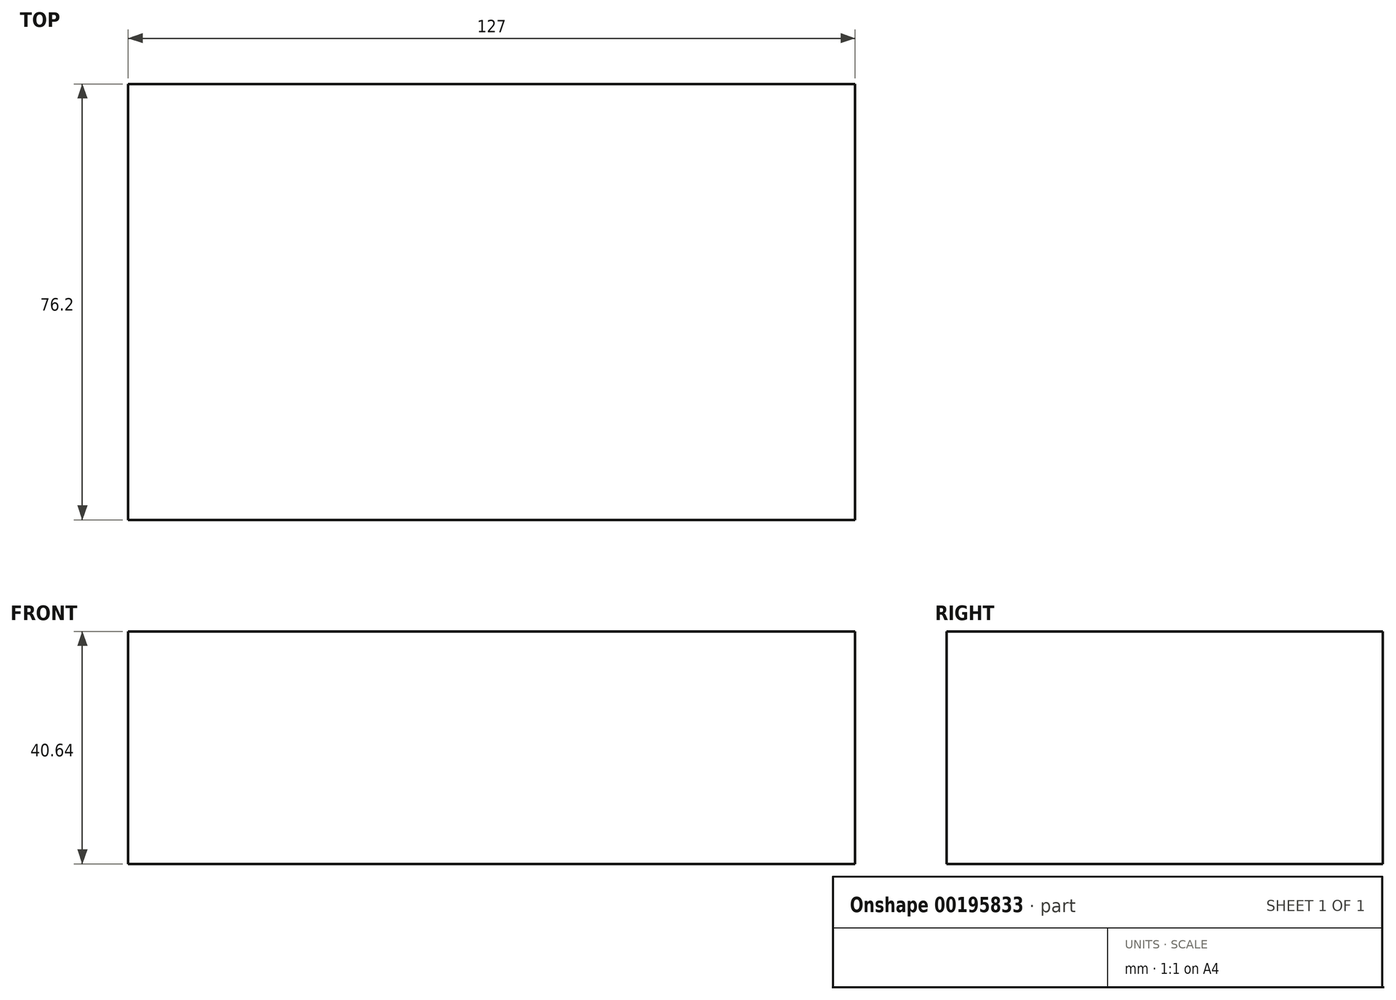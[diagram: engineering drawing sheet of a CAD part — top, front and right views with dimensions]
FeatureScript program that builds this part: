
annotation { "Feature Type Name" : "Feature", "Feature Type Description" : "" }
export const myFeature = defineFeature(function(context is Context, id is Id, definition is map)
    precondition{}
    {
        {
            var Q0;
            Q0=qCreatedBy(makeId("Top.planeOp"),FACE);
            var sketch = newSketch(context, id + "F0", { "sketchPlane" : qUnion([Q0])});
            skLineSegment(sketch, "E0.bottom", {"start": v(-63.5, 38.1) * mm, "end": v(63.5, 38.1) * mm});
            skLineSegment(sketch, "E0.top", {"start": v(-63.5, -38.1) * mm, "end": v(63.5, -38.1) * mm});
            skLineSegment(sketch, "E0.left", {"start": v(-63.5, 38.1) * mm, "end": v(-63.5, -38.1) * mm});
            skLineSegment(sketch, "E0.right", {"start": v(63.5, 38.1) * mm, "end": v(63.5, -38.1) * mm});
            skPoint(sketch, "E0.middle", {"position": v(0, 0) * mm});
            skSolve(sketch);
        }
        {
            var Q0;
            Q0=makeQuery(id+"F0.imprint","IMPRINT",FACE,{"disambiguationData":[TD([[makeQuery(id+"F0.imprint","IMPRINT",EDGE,{"derivedFrom":sQuery(id+"F0.wireOp",EDGE,"E0.bottom")}),-1.0]])]});
            extrude(context, id + "F1", {"entities" : qUnion([Q0]), "depth" : 40.64 * mm});
        }
    });
